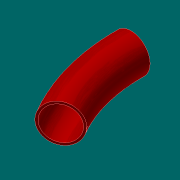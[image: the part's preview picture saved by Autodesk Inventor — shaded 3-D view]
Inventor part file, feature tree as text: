
AUTODESK INVENTOR PART (.ipt)
format: ipt  version: 2017.3 (Build 213257000, 257)  size: 141,824 bytes
history: native  units: in
note: dims shown in document units (in); Inventor stores cm internally (conversion verified against a paired STEP export)
features: other x3, revolve x1, sketch x1
ambient origin geometry x8: Origin, YZ Plane, XZ Plane, XY Plane, X Axis, Y Axis, Z Axis, Center Point
bodies: Solid1 (feature_tree)
feature tree (5):
  other  "A1-19027-100-08 HCWI elbow - center.ipt"
  revolve  "Revolution1"  [1 undecoded]
  other  "Solid1::A1-19027-100-08 HCWI elbow - center.ipt"
  other  "TaggingFeature1"
  sketch  "Sketch1"  dims[d0=0.3937in d1=2.0in d2=0.2096in d3=0.0034in]
note: 1 required parameter value undecoded (feature->parameter linkage not recoverable at this tier; creation-order binding heuristic only, values carry confidence <= 0.55)
